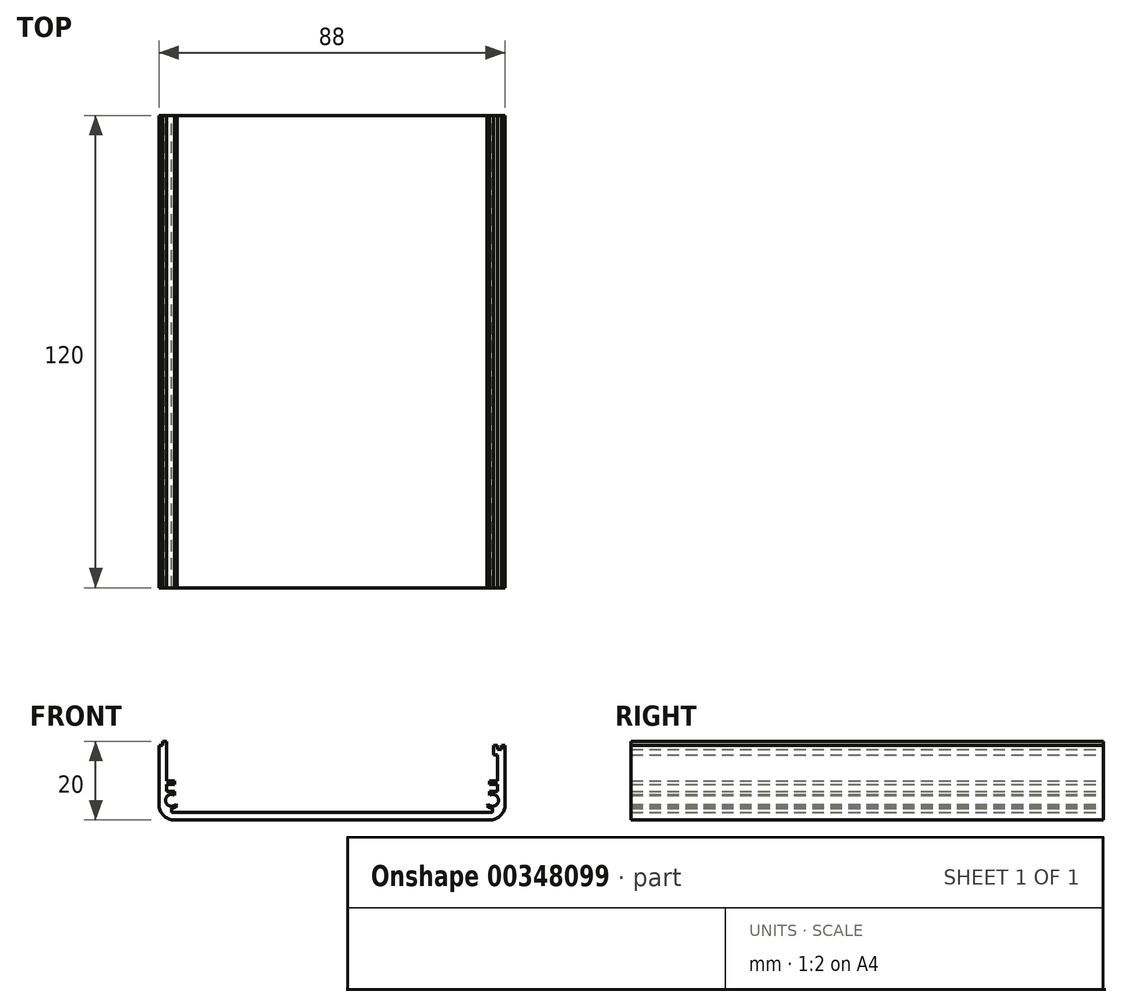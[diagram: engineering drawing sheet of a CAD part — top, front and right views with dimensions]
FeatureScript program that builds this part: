
annotation { "Feature Type Name" : "Feature", "Feature Type Description" : "" }
export const myFeature = defineFeature(function(context is Context, id is Id, definition is map)
    precondition{}
    {
        {
            var Q0;
            Q0=qCreatedBy(makeId("Front.planeOp"),FACE);
            var sketch = newSketch(context, id + "F0", { "sketchPlane" : qUnion([Q0])});
            skLineSegment(sketch, "E0.top", {"start": v(-40, 0) * mm, "end": v(40, 0) * mm});
            skLineSegment(sketch, "E0.left", {"start": v(-44, 19) * mm, "end": v(-44, 4) * mm});
            skLineSegment(sketch, "E0.right", {"start": v(44, 19) * mm, "end": v(44, 4) * mm});
            skPoint(sketch, "E1.visualSharp", {"position": v(-44, 0) * mm});
            skArc(sketch, "E1.filletArc", {"start": v(-44, 4) * mm, "mid": v(-42.83, 1.17) * mm, "end": v(-40, 0) * mm});
            skPoint(sketch, "E2.visualSharp", {"position": v(44, 0) * mm});
            skArc(sketch, "E2.filletArc", {"start": v(40, 0) * mm, "mid": v(42.83, 1.17) * mm, "end": v(44, 4) * mm});
            skLineSegment(sketch, "E3", {"start": v(-44, 19) * mm, "end": v(-43, 19) * mm});
            skLineSegment(sketch, "E4", {"start": v(-43, 19) * mm, "end": v(-43, 20) * mm});
            skLineSegment(sketch, "E5", {"start": v(-43, 20) * mm, "end": v(-42, 20) * mm});
            skLineSegment(sketch, "E6", {"start": v(-42, 20) * mm, "end": v(-42, 10) * mm});
            skLineSegment(sketch, "E7", {"start": v(-42, 10) * mm, "end": v(-40, 10) * mm});
            skLineSegment(sketch, "E8", {"start": v(-40, 10) * mm, "end": v(-40, 9) * mm});
            skLineSegment(sketch, "E9", {"start": v(-40, 9) * mm, "end": v(-42, 9) * mm});
            skLineSegment(sketch, "E10", {"start": v(-42, 9) * mm, "end": v(-42, 7.3) * mm});
            skLineSegment(sketch, "E11", {"start": v(-42, 7.3) * mm, "end": v(-40, 7.3) * mm});
            skLineSegment(sketch, "E12", {"start": v(44, 19) * mm, "end": v(43, 19) * mm});
            skLineSegment(sketch, "E13", {"start": v(43, 19) * mm, "end": v(43, 18) * mm});
            skLineSegment(sketch, "E14", {"start": v(43, 18) * mm, "end": v(42, 18) * mm});
            skLineSegment(sketch, "E15", {"start": v(42, 18) * mm, "end": v(42, 19) * mm});
            skLineSegment(sketch, "E16", {"start": v(42, 19) * mm, "end": v(41, 19) * mm});
            skLineSegment(sketch, "E17", {"start": v(41, 19) * mm, "end": v(41, 16.5) * mm});
            skLineSegment(sketch, "E18", {"start": v(41, 16.5) * mm, "end": v(42, 16.5) * mm});
            skArc(sketch, "E19", {"start": v(-40, 6.27) * mm, "mid": v(-42.29, 4.8) * mm, "end": v(-39.68, 4) * mm});
            skArc(sketch, "E20", {"start": v(-39.33, 3.65) * mm, "mid": v(-40, 3.17) * mm, "end": v(-40.8, 3) * mm});
            skLineSegment(sketch, "E21", {"start": v(-40.8, 3) * mm, "end": v(-40.8, 2) * mm});
            skLineSegment(sketch, "E22", {"start": v(-40.8, 2) * mm, "end": v(40.8, 2) * mm});
            skLineSegment(sketch, "E23", {"start": v(-39.68, 4) * mm, "end": v(-39.33, 3.65) * mm});
            skLineSegment(sketch, "E24.MirrorCS", {"start": v(42, 10) * mm, "end": v(40, 10) * mm});
            skLineSegment(sketch, "E25.MirrorCS", {"start": v(40, 9) * mm, "end": v(42, 9) * mm});
            skLineSegment(sketch, "E26.MirrorCS", {"start": v(40, 10) * mm, "end": v(40, 9) * mm});
            skLineSegment(sketch, "E27.MirrorCS", {"start": v(42, 9) * mm, "end": v(42, 7.3) * mm});
            skLineSegment(sketch, "E28.MirrorCS", {"start": v(42, 7.3) * mm, "end": v(40, 7.3) * mm});
            skArc(sketch, "E29.MirrorCS", {"start": v(40, 6.27) * mm, "mid": v(42.29, 4.8) * mm, "end": v(39.68, 4) * mm});
            skLineSegment(sketch, "E30", {"start": v(42, 16.5) * mm, "end": v(42, 10) * mm});
            skLineSegment(sketch, "E31.MirrorCS", {"start": v(39.68, 4) * mm, "end": v(39.33, 3.65) * mm});
            skArc(sketch, "E32.MirrorCS", {"start": v(39.33, 3.65) * mm, "mid": v(40, 3.17) * mm, "end": v(40.8, 3) * mm});
            skLineSegment(sketch, "E33.MirrorCS", {"start": v(40.8, 3) * mm, "end": v(40.8, 2) * mm});
            skLineSegment(sketch, "E34", {"start": v(-40, 7.3) * mm, "end": v(-40, 6.27) * mm});
            skLineSegment(sketch, "E35.MirrorCS", {"start": v(40, 7.3) * mm, "end": v(40, 6.27) * mm});
            skSolve(sketch);
        }
        {
            var Q0;
            Q0 = qSketchRegion(id + "F0", true);
            extrude(context, id + "F1", {"entities" : qUnion([Q0]), "depth" : 120 * mm});
        }
    });
